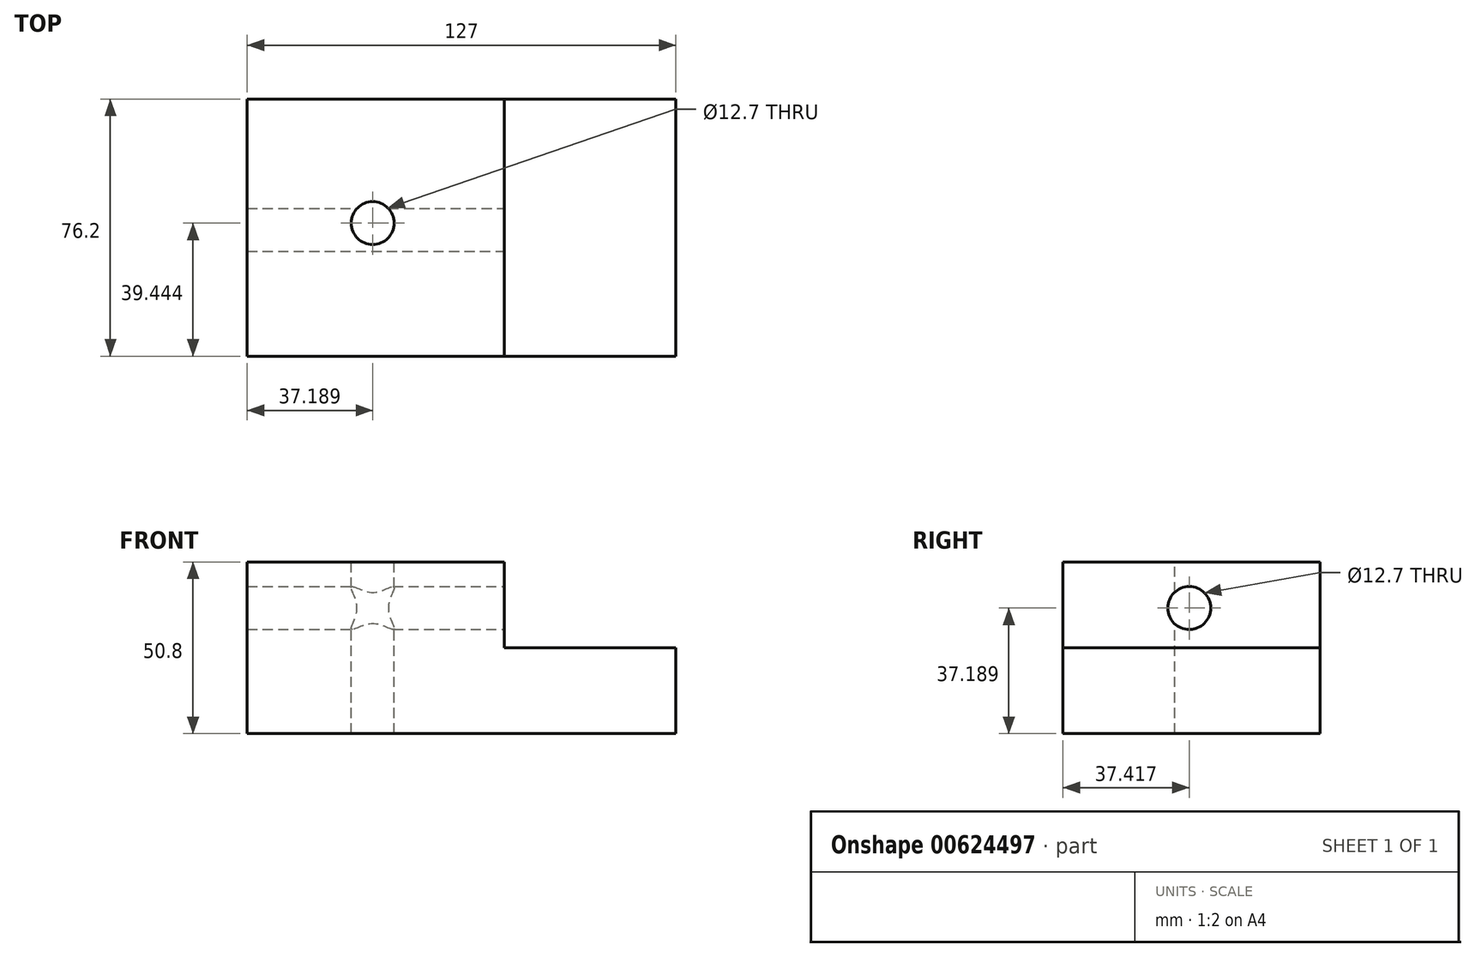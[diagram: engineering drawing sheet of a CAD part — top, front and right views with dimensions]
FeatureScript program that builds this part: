
annotation { "Feature Type Name" : "Feature", "Feature Type Description" : "" }
export const myFeature = defineFeature(function(context is Context, id is Id, definition is map)
    precondition{}
    {
        {
            var Q0;
            Q0=qCreatedBy(makeId("Front.planeOp"),FACE);
            var sketch = newSketch(context, id + "F0", { "sketchPlane" : qUnion([Q0])});
            skLineSegment(sketch, "E0.bottom", {"start": v(0, 0) * mm, "end": v(127, 0) * mm});
            skLineSegment(sketch, "E0.top", {"start": v(0, 50.8) * mm, "end": v(127, 50.8) * mm});
            skLineSegment(sketch, "E0.left", {"start": v(0, 0) * mm, "end": v(0, 50.8) * mm});
            skLineSegment(sketch, "E0.right", {"start": v(127, 0) * mm, "end": v(127, 50.8) * mm});
            skLineSegment(sketch, "E1.bottom", {"start": v(127, 50.8) * mm, "end": v(76.2, 50.8) * mm});
            skLineSegment(sketch, "E1.top", {"start": v(127, 25.4) * mm, "end": v(76.2, 25.4) * mm});
            skLineSegment(sketch, "E1.left", {"start": v(127, 50.8) * mm, "end": v(127, 25.4) * mm});
            skLineSegment(sketch, "E1.right", {"start": v(76.2, 50.8) * mm, "end": v(76.2, 25.4) * mm});
            skSolve(sketch);
        }
        {
            var Q0;
            Q0=makeQuery(id+"F0.imprint","IMPRINT",FACE,{"disambiguationData":[TD([[makeQuery(id+"F0.imprint","IMPRINT",EDGE,{"derivedFrom":sQuery(id+"F0.wireOp",EDGE,"E0.bottom")}),1.0]])]});
            extrude(context, id + "F1", {"entities" : qUnion([Q0]), "depth" : 76.2 * mm, "offsetDistance" : 25.4 * mm});
        }
        {
            var Q0;
            Q0=makeQuery(id+"F1.opExtrude","SWEPT_FACE",FACE,{"disambiguationData":[OSD([sQuery(id+"F0.wireOp",EDGE,"E1.right")])]});
            var sketch = newSketch(context, id + "F2", { "sketchPlane" : qUnion([Q0])});
            skCircle(sketch, "E2", {"center": v(-38.78, 37.19) * mm, "radius": 6.62 * mm});
            skSolve(sketch);
        }
        {
            var Q0;
            Q0=sQuery(id+"F2.wireOp",VERTEX,"E2.center");
            var Q1;
            Q1=makeQuery(id+"F1.opExtrude","SWEPT_BODY",BODY,{"disambiguationData":[OSD([sQuery(id+"F0.wireOp",EDGE,"E0.bottom"),sQuery(id+"F0.wireOp",EDGE,"E0.top"),sQuery(id+"F0.wireOp",EDGE,"E0.left"),sQuery(id+"F0.wireOp",EDGE,"E0.right"),sQuery(id+"F0.wireOp",EDGE,"E1.top"),sQuery(id+"F0.wireOp",EDGE,"E1.right")])]});
            hole(context, id + "F3", {"style" : HoleStyle.SIMPLE, "endStyle" : HoleEndStyle.THROUGH, "holeDiameter" : 12.7 * mm, "majorDiameter" : 6.35 * mm, "isTappedThrough" : true, "tappedDepth" : 12.7 * mm, "tapClearance" : 3, "locations" : qUnion([Q0]), "scope" : qUnion([Q1])});
        }
        {
            var Q0;
            Q0=makeQuery(id+"F1.opExtrude","SWEPT_FACE",FACE,{"disambiguationData":[OSD([sQuery(id+"F0.wireOp",EDGE,"E0.top")])]});
            var sketch = newSketch(context, id + "F4", { "sketchPlane" : qUnion([Q0])});
            skPoint(sketch, "E3", {"position": v(37.19, -36.76) * mm});
            skSolve(sketch);
        }
        {
            var Q0;
            Q0=sQuery(id+"F4.wireOp",VERTEX,"E3");
            var Q1;
            Q1=makeQuery(id+"F1.opExtrude","SWEPT_BODY",BODY,{"disambiguationData":[OSD([sQuery(id+"F0.wireOp",EDGE,"E0.bottom"),sQuery(id+"F0.wireOp",EDGE,"E0.top"),sQuery(id+"F0.wireOp",EDGE,"E0.left"),sQuery(id+"F0.wireOp",EDGE,"E0.right"),sQuery(id+"F0.wireOp",EDGE,"E1.top"),sQuery(id+"F0.wireOp",EDGE,"E1.right")])]});
            hole(context, id + "F5", {"style" : HoleStyle.SIMPLE, "endStyle" : HoleEndStyle.THROUGH, "holeDiameter" : 12.7 * mm, "majorDiameter" : 6.35 * mm, "isTappedThrough" : true, "tappedDepth" : 12.7 * mm, "tapClearance" : 3, "locations" : qUnion([Q0]), "scope" : qUnion([Q1])});
        }
    });
